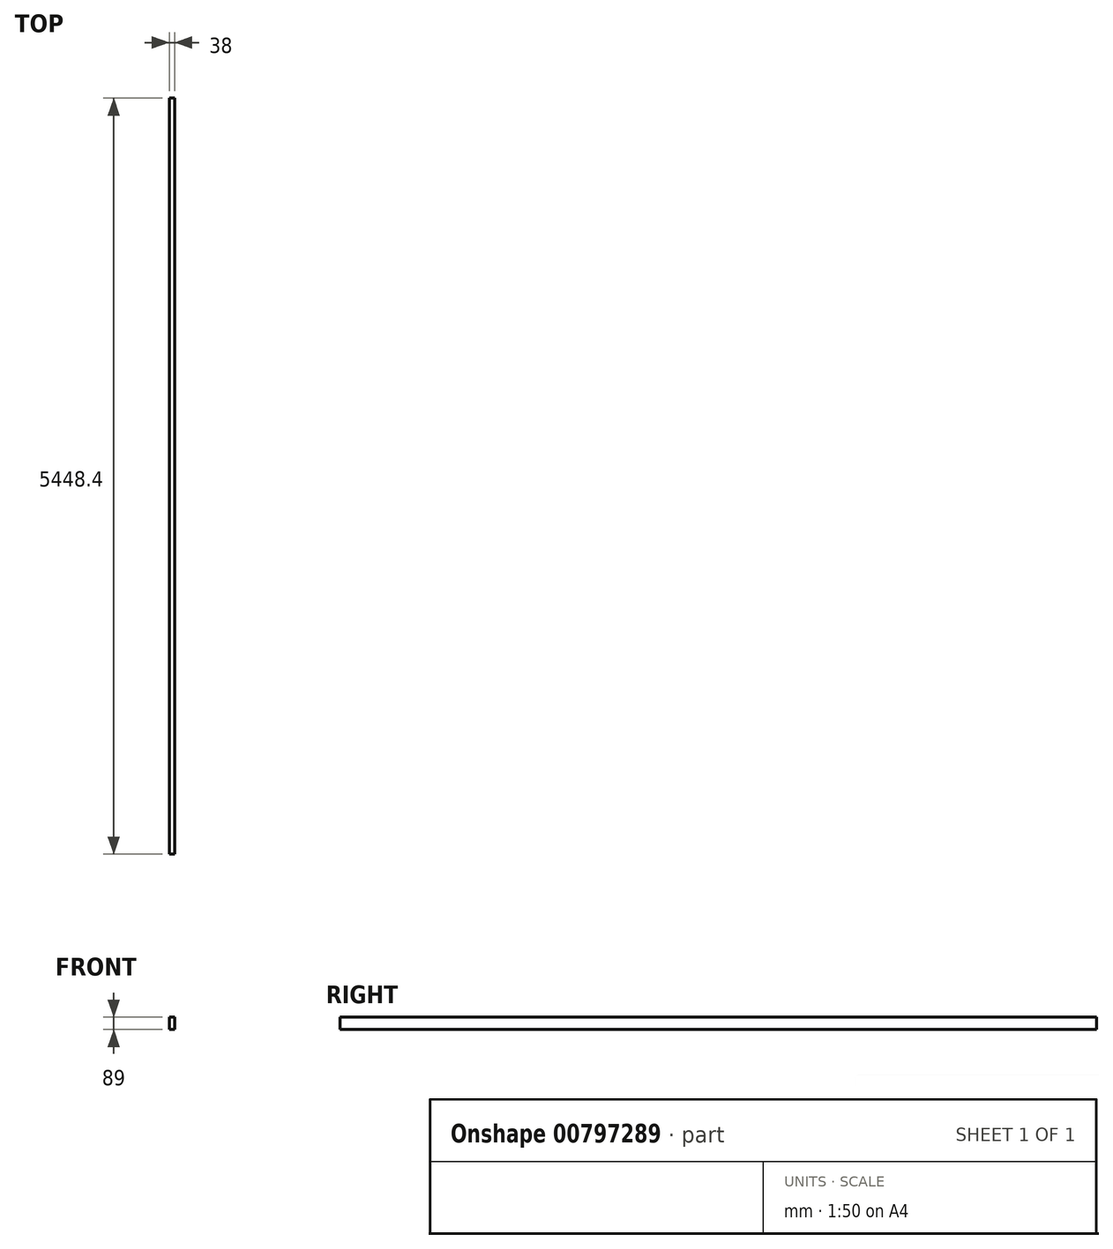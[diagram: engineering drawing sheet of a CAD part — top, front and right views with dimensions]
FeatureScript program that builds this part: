
annotation { "Feature Type Name" : "Feature", "Feature Type Description" : "" }
export const myFeature = defineFeature(function(context is Context, id is Id, definition is map)
    precondition{}
    {
        {
            var Q0;
            Q0=qCreatedBy(makeId("Front.planeOp"),FACE);
            var sketch = newSketch(context, id + "F0", { "sketchPlane" : qUnion([Q0])});
            skLineSegment(sketch, "E0.bottom", {"start": v(19, 44.5) * mm, "end": v(-19, 44.5) * mm});
            skLineSegment(sketch, "E0.top", {"start": v(19, -44.5) * mm, "end": v(-19, -44.5) * mm});
            skLineSegment(sketch, "E0.left", {"start": v(19, 44.5) * mm, "end": v(19, -44.5) * mm});
            skLineSegment(sketch, "E0.right", {"start": v(-19, 44.5) * mm, "end": v(-19, -44.5) * mm});
            skPoint(sketch, "E0.middle", {"position": v(0, 0) * mm});
            skSolve(sketch);
        }
        {
            var Q0;
            Q0 = qSketchRegion(id + "F0", true);
            extrude(context, id + "F1", {"entities" : qUnion([Q0]), "depth" : 5448.4 * mm, "offsetDistance" : 25 * mm, "symmetric" : true});
        }
    });
